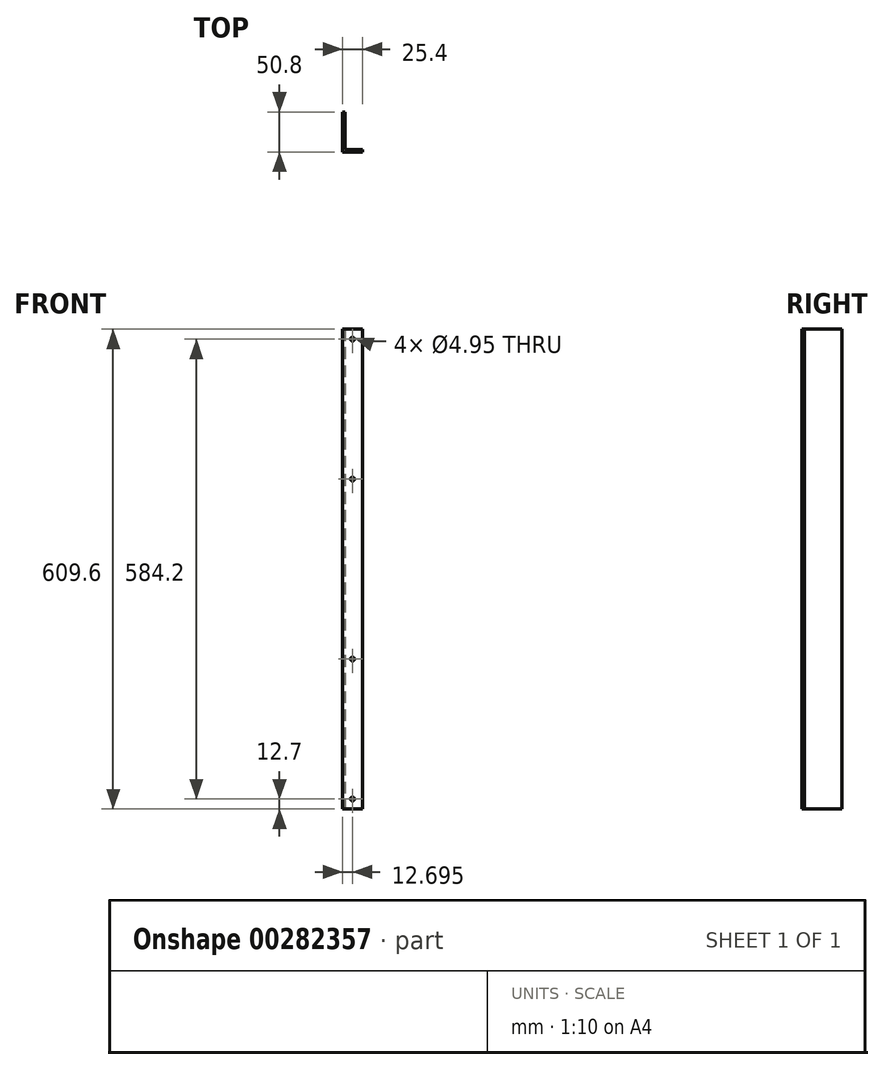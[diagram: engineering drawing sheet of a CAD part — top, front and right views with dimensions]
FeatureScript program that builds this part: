
annotation { "Feature Type Name" : "Feature", "Feature Type Description" : "" }
export const myFeature = defineFeature(function(context is Context, id is Id, definition is map)
    precondition{}
    {
        {
            var Q0;
            Q0=qCreatedBy(makeId("Top.planeOp"),FACE);
            var sketch = newSketch(context, id + "F0", { "sketchPlane" : qUnion([Q0])});
            skLineSegment(sketch, "E0", {"start": v(0, 47.62) * mm, "end": v(-3.18, 47.62) * mm});
            skLineSegment(sketch, "E1", {"start": v(-3.18, 47.62) * mm, "end": v(-3.18, -3.18) * mm});
            skLineSegment(sketch, "E2", {"start": v(-3.17, -3.18) * mm, "end": v(22.22, -3.18) * mm});
            skLineSegment(sketch, "E3", {"start": v(22.22, -3.17) * mm, "end": v(22.22, 0) * mm});
            skLineSegment(sketch, "E4", {"start": v(0, 0) * mm, "end": v(0, 47.62) * mm});
            skLineSegment(sketch, "E5", {"start": v(0, 0) * mm, "end": v(22.22, 0) * mm});
            skSolve(sketch);
        }
        {
            var Q0;
            Q0 = qSketchRegion(id + "F0", true);
            extrude(context, id + "F1", {"entities" : qUnion([Q0]), "depth" : 609.6 * mm});
        }
        {
            var Q0;
            Q0=makeQuery(id+"F1.opExtrude","SWEPT_FACE",FACE,{"disambiguationData":[OSD([sQuery(id+"F0.wireOp",EDGE,"E2")])]});
            var sketch = newSketch(context, id + "F2", { "sketchPlane" : qUnion([Q0])});
            skCircle(sketch, "E6", {"center": v(9.53, 12.7) * mm, "radius": 2.48 * mm});
            skCircle(sketch, "E7", {"center": v(9.53, 190.5) * mm, "radius": 2.48 * mm});
            skCircle(sketch, "E8", {"center": v(9.53, 419.1) * mm, "radius": 2.48 * mm});
            skCircle(sketch, "E9", {"center": v(9.53, 596.9) * mm, "radius": 2.48 * mm});
            skLineSegment(sketch, "E10", {"start": v(9.53, 12.7) * mm, "end": v(9.53, 190.5) * mm, "construction": true});
            skLineSegment(sketch, "E11", {"start": v(9.53, 419.1) * mm, "end": v(9.53, 596.9) * mm, "construction": true});
            skSolve(sketch);
        }
        {
            var Q0;
            Q0 = qSketchRegion(id + "F2", true);
            extrude(context, id + "F3", {"entities" : qUnion([Q0]), "operationType" : NewBodyOperationType.REMOVE, "endBound" : BoundingType.THROUGH_ALL, "oppositeDirection" : true, "depth" : 25.4 * mm});
        }
    });
